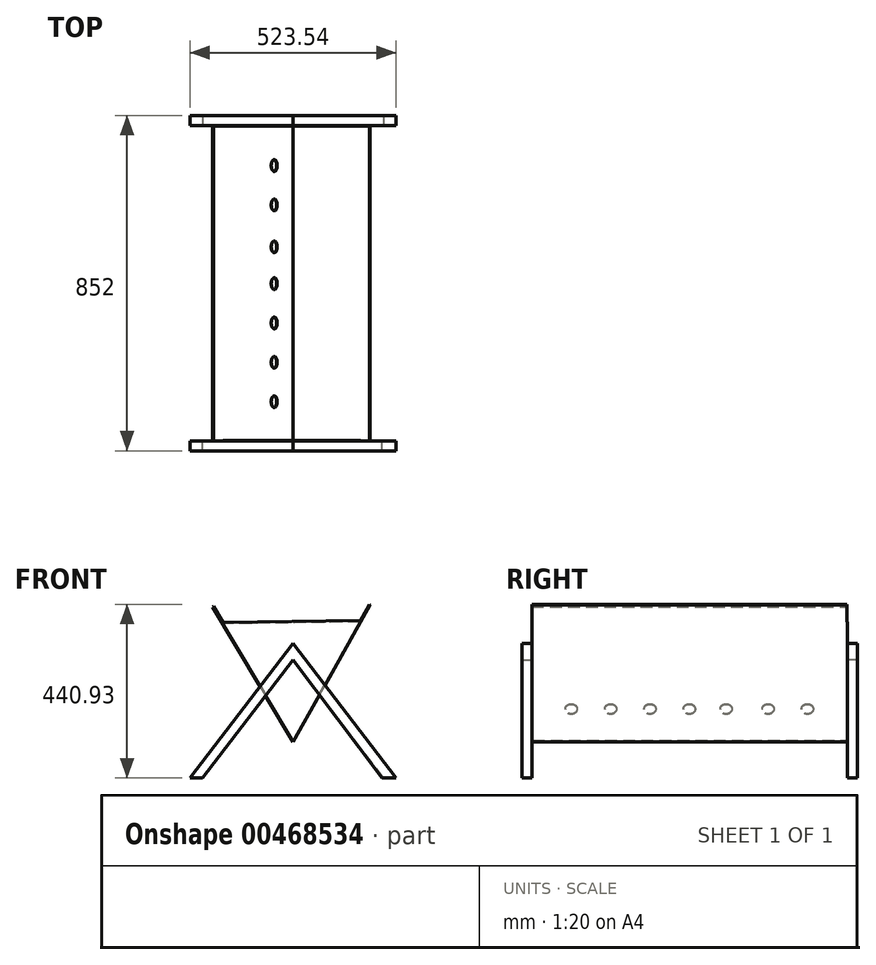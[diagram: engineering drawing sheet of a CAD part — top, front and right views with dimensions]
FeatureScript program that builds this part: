
annotation { "Feature Type Name" : "Feature", "Feature Type Description" : "" }
export const myFeature = defineFeature(function(context is Context, id is Id, definition is map)
    precondition{}
    {
        {
            var Q0;
            Q0=qCreatedBy(makeId("Front.planeOp"),FACE);
            var sketch = newSketch(context, id + "F0", { "sketchPlane" : qUnion([Q0])});
            skLineSegment(sketch, "E0", {"start": v(-204.18, 326.74) * mm, "end": v(0, -17.22) * mm});
            skLineSegment(sketch, "E1", {"start": v(0, -17.22) * mm, "end": v(195.8, 331.58) * mm});
            skLineSegment(sketch, "E2", {"start": v(195.8, 331.58) * mm, "end": v(194.05, 332.56) * mm});
            skLineSegment(sketch, "E3", {"start": v(194.05, 332.56) * mm, "end": v(0, -13.14) * mm});
            skLineSegment(sketch, "E4", {"start": v(0, -13.14) * mm, "end": v(-202.42, 327.69) * mm});
            skLineSegment(sketch, "E5", {"start": v(-202.42, 327.69) * mm, "end": v(-204.18, 326.74) * mm});
            skSolve(sketch);
        }
        {
            var Q0;
            Q0 = qSketchRegion(id + "F0", true);
            extrude(context, id + "F1", {"entities" : qUnion([Q0]), "depth" : 800 * mm});
        }
        {
            var Q0;
            Q0=makeQuery(id+"F1.opExtrude","CAP_FACE",FACE,{"disambiguationData":[OSD([sQuery(id+"F0.wireOp",EDGE,"E0"),sQuery(id+"F0.wireOp",EDGE,"E1"),sQuery(id+"F0.wireOp",EDGE,"E2"),sQuery(id+"F0.wireOp",EDGE,"E3"),sQuery(id+"F0.wireOp",EDGE,"E4"),sQuery(id+"F0.wireOp",EDGE,"E5")])],"isStart":false});
            var sketch = newSketch(context, id + "F2", { "sketchPlane" : qUnion([Q0])});
            skLineSegment(sketch, "E6", {"start": v(171.32, 292.07) * mm, "end": v(0, -13.14) * mm});
            skLineSegment(sketch, "E7", {"start": v(0, -13.14) * mm, "end": v(-180.44, 286.76) * mm});
            skLineSegment(sketch, "E8", {"start": v(-180.44, 286.76) * mm, "end": v(171.32, 292.07) * mm});
            skSolve(sketch);
        }
        {
            var Q0;
            Q0 = qSketchRegion(id + "F2", true);
            extrude(context, id + "F3", {"entities" : qUnion([Q0]), "operationType" : NewBodyOperationType.ADD, "oppositeDirection" : true, "depth" : 2 * mm});
        }
        {
            var Q0;
            Q0=makeQuery(id+"F1.opExtrude","CAP_FACE",FACE,{"disambiguationData":[OSD([sQuery(id+"F0.wireOp",EDGE,"E0"),sQuery(id+"F0.wireOp",EDGE,"E1"),sQuery(id+"F0.wireOp",EDGE,"E2"),sQuery(id+"F0.wireOp",EDGE,"E3"),sQuery(id+"F0.wireOp",EDGE,"E4"),sQuery(id+"F0.wireOp",EDGE,"E5")])],"isStart":true});
            var sketch = newSketch(context, id + "F4", { "sketchPlane" : qUnion([Q0])});
            skLineSegment(sketch, "E9", {"start": v(0, -17.22) * mm, "end": v(-171.32, 287.98) * mm});
            skLineSegment(sketch, "E10", {"start": v(0, -17.22) * mm, "end": v(178.65, 283.74) * mm});
            skLineSegment(sketch, "E11", {"start": v(-171.32, 287.98) * mm, "end": v(178.65, 283.74) * mm});
            skSolve(sketch);
        }
        {
            var Q0;
            Q0 = qSketchRegion(id + "F4", true);
            extrude(context, id + "F5", {"entities" : qUnion([Q0]), "operationType" : NewBodyOperationType.ADD, "depth" : 2 * mm});
        }
        {
            var Q0;
            Q0=makeQuery(id+"F5.opExtrude","CAP_FACE",FACE,{"disambiguationData":[OSD([sQuery(id+"F4.wireOp",EDGE,"E9"),sQuery(id+"F4.wireOp",EDGE,"E10"),sQuery(id+"F4.wireOp",EDGE,"E11")])],"isStart":false});
            var sketch = newSketch(context, id + "F6", { "sketchPlane" : qUnion([Q0])});
            skLineSegment(sketch, "E12", {"start": v(0, -17.22) * mm, "end": v(0, 285.9) * mm, "construction": true});
            skPoint(sketch, "E13", {"position": v(0, 232.78) * mm});
            skLineSegment(sketch, "E14", {"start": v(0, 232.78) * mm, "end": v(-261.77, -108.37) * mm});
            skLineSegment(sketch, "E15", {"start": v(-261.77, -108.37) * mm, "end": v(-230.26, -108.37) * mm});
            skLineSegment(sketch, "E16", {"start": v(-230.26, -108.37) * mm, "end": v(0, 191.7) * mm});
            skLineSegment(sketch, "E17", {"start": v(0, 191.7) * mm, "end": v(230.26, -108.37) * mm});
            skLineSegment(sketch, "E18", {"start": v(230.26, -108.37) * mm, "end": v(261.77, -108.37) * mm});
            skLineSegment(sketch, "E19", {"start": v(261.77, -108.37) * mm, "end": v(0, 232.78) * mm});
            skSolve(sketch);
        }
        {
            var Q0;
            {var subQ0=sQuery(id+"F6.wireOp",EDGE,"E15");Q0=makeQuery(id+"F6.imprint","IMPRINT",FACE,{"disambiguationData":[TD([[makeQuery(id+"F6.imprint","IMPRINT",EDGE,{"derivedFrom":subQ0}),1.0]])]});}
            var Q1;
            {var subQ0=sQuery(id+"F6.wireOp",EDGE,"E18");Q1=makeQuery(id+"F6.imprint","IMPRINT",FACE,{"disambiguationData":[TD([[makeQuery(id+"F6.imprint","IMPRINT",EDGE,{"derivedFrom":subQ0}),1.0]])]});}
            var Q2;
            {var subQ0=sQuery(id+"F6.wireOp",EDGE,"E19");var subQ1=sQuery(id+"F6.wireOp",EDGE,"E14");var subQ2=makeQuery(id+"F6.imprint","INTERSECT",VERTEX,{"derivedFrom":[subQ1,subQ0]});Q2=makeQuery(id+"F6.imprint","IMPRINT",FACE,{"disambiguationData":[TD([[makeQuery(id+"F6.imprint","IMPRINT",EDGE,{"disambiguationData":[TD([[subQ2,-1.0]])],"derivedFrom":subQ1}),1.0]])]});}
            extrude(context, id + "F7", {"entities" : qUnion([Q0, Q1, Q2]), "operationType" : NewBodyOperationType.ADD, "depth" : 25 * mm});
        }
        {
            var Q0;
            Q0=makeQuery(id+"F3.boolean.opBoolean","MERGE",FACE,{"derivedFrom":[makeQuery(id+"F1.opExtrude","CAP_FACE",FACE,{"disambiguationData":[OSD([sQuery(id+"F0.wireOp",EDGE,"E0"),sQuery(id+"F0.wireOp",EDGE,"E1"),sQuery(id+"F0.wireOp",EDGE,"E2"),sQuery(id+"F0.wireOp",EDGE,"E3"),sQuery(id+"F0.wireOp",EDGE,"E4"),sQuery(id+"F0.wireOp",EDGE,"E5")])],"isStart":false}),makeQuery(id+"F3.opExtrude","CAP_FACE",FACE,{"disambiguationData":[OSD([sQuery(id+"F2.wireOp",EDGE,"E6"),sQuery(id+"F2.wireOp",EDGE,"E7"),sQuery(id+"F2.wireOp",EDGE,"E8")])],"isStart":true})]});
            var sketch = newSketch(context, id + "F8", { "sketchPlane" : qUnion([Q0])});
            skLineSegment(sketch, "E20", {"start": v(0, -17.22) * mm, "end": v(0, 287.5) * mm, "construction": true});
            skPoint(sketch, "E21", {"position": v(0, 232.78) * mm});
            skLineSegment(sketch, "E22", {"start": v(0, 232.78) * mm, "end": v(-261.77, -108.37) * mm});
            skLineSegment(sketch, "E23", {"start": v(-261.77, -108.37) * mm, "end": v(-230.26, -108.37) * mm});
            skLineSegment(sketch, "E24", {"start": v(-230.26, -108.37) * mm, "end": v(0, 191.7) * mm});
            skLineSegment(sketch, "E25", {"start": v(0, 191.7) * mm, "end": v(225.85, -108.37) * mm});
            skLineSegment(sketch, "E26", {"start": v(225.85, -108.37) * mm, "end": v(261.77, -108.37) * mm});
            skLineSegment(sketch, "E27", {"start": v(261.77, -108.37) * mm, "end": v(0, 232.78) * mm});
            skSolve(sketch);
        }
        {
            var Q0;
            {var subQ0=sQuery(id+"F8.wireOp",EDGE,"E27");var subQ1=sQuery(id+"F8.wireOp",EDGE,"E22");var subQ2=makeQuery(id+"F8.imprint","INTERSECT",VERTEX,{"derivedFrom":[subQ1,subQ0]});Q0=makeQuery(id+"F8.imprint","IMPRINT",FACE,{"disambiguationData":[TD([[makeQuery(id+"F8.imprint","IMPRINT",EDGE,{"disambiguationData":[TD([[subQ2,-1.0]])],"derivedFrom":subQ1}),1.0]])]});}
            var Q1;
            {var subQ0=sQuery(id+"F8.wireOp",EDGE,"E26");Q1=makeQuery(id+"F8.imprint","IMPRINT",FACE,{"disambiguationData":[TD([[makeQuery(id+"F8.imprint","IMPRINT",EDGE,{"derivedFrom":subQ0}),1.0]])]});}
            var Q2;
            {var subQ0=sQuery(id+"F8.wireOp",EDGE,"E23");Q2=makeQuery(id+"F8.imprint","IMPRINT",FACE,{"disambiguationData":[TD([[makeQuery(id+"F8.imprint","IMPRINT",EDGE,{"derivedFrom":subQ0}),1.0]])]});}
            extrude(context, id + "F9", {"entities" : qUnion([Q0, Q1, Q2]), "operationType" : NewBodyOperationType.ADD, "depth" : 25 * mm});
        }
        {
            var Q0;
            Q0=makeQuery(id+"F5.boolean.opBoolean","MERGE",FACE,{"derivedFrom":[makeQuery(id+"F1.opExtrude","SWEPT_FACE",FACE,{"disambiguationData":[OSD([sQuery(id+"F0.wireOp",EDGE,"E0")])]}),makeQuery(id+"F5.opExtrude","SWEPT_FACE",FACE,{"disambiguationData":[OSD([sQuery(id+"F4.wireOp",EDGE,"E10")])]})]});
            var sketch = newSketch(context, id + "F10", { "sketchPlane" : qUnion([Q0])});
            skSolve(sketch);
        }
        {
            var Q0;
            {var subQ0=sQuery(id+"F0.wireOp",EDGE,"E0");Q0=makeQuery(id+"F10.imprint","IMPRINT",FACE,{"disambiguationData":[TD([[makeQuery(id+"F10.imprint","IMPRINT",EDGE,{"derivedFrom":makeQuery(id+"F1.opExtrude","CAP_EDGE",EDGE,{"disambiguationData":[OSD([subQ0])],"isStart":true})}),1.0]])]});}
            var sketch = newSketch(context, id + "F11", { "sketchPlane" : qUnion([Q0])});
            skLineSegment(sketch, "E28", {"start": v(0, 0) * mm, "end": v(0, 82.12) * mm, "construction": true});
            skLineSegment(sketch, "E29", {"start": v(0, 82.12) * mm, "end": v(800, 82.12) * mm, "construction": true});
            skLineSegment(sketch, "E30", {"start": v(800, 82.12) * mm, "end": v(800, 0) * mm, "construction": true});
            skCircle(sketch, "E31", {"center": v(400, 82.12) * mm, "radius": 15 * mm});
            skCircle(sketch, "E32", {"center": v(306.6, 82.12) * mm, "radius": 15 * mm});
            skCircle(sketch, "E33", {"center": v(200, 82.12) * mm, "radius": 15 * mm});
            skCircle(sketch, "E34", {"center": v(100, 82.12) * mm, "radius": 15 * mm});
            skCircle(sketch, "E35", {"center": v(500, 82.12) * mm, "radius": 15 * mm});
            skCircle(sketch, "E36", {"center": v(600, 82.12) * mm, "radius": 15 * mm});
            skCircle(sketch, "E37", {"center": v(700, 82.12) * mm, "radius": 15 * mm});
            skSolve(sketch);
        }
        {
            var Q0;
            Q0 = qSketchRegion(id + "F11", true);
            extrude(context, id + "F12", {"entities" : qUnion([Q0]), "operationType" : NewBodyOperationType.REMOVE, "oppositeDirection" : true, "depth" : 10 * mm});
        }
    });
